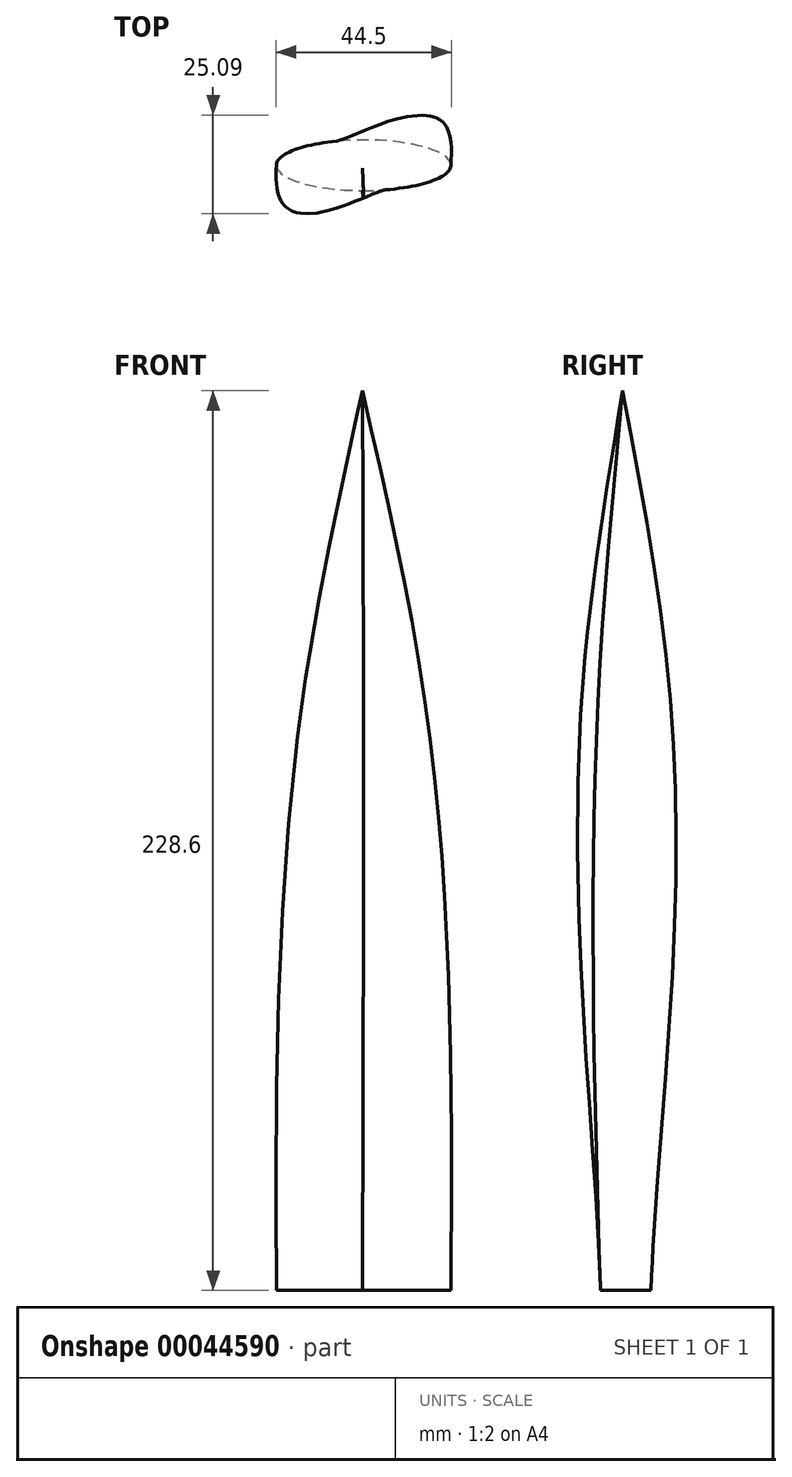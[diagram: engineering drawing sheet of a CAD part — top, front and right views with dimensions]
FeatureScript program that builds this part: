
annotation { "Feature Type Name" : "Feature", "Feature Type Description" : "" }
export const myFeature = defineFeature(function(context is Context, id is Id, definition is map)
    precondition{}
    {
        {
            var Q0;
            Q0=qCreatedBy(makeId("Top.planeOp"),FACE);
            cPlane(context, id + "F0", {"entities" : qUnion([Q0]), "cplaneType" : CPlaneType.OFFSET, "offset" : 152.4 * mm, "width" : 152.4 * mm, "height" : 152.4 * mm});
        }
        {
            var Q0;
            Q0=qCreatedBy(id+"F0.planeOp",FACE);
            cPlane(context, id + "F1", {"entities" : qUnion([Q0]), "cplaneType" : CPlaneType.OFFSET, "offset" : 76.2 * mm, "width" : 152.4 * mm, "height" : 152.4 * mm});
        }
        {
            var Q0;
            Q0=qCreatedBy(makeId("Top.planeOp"),FACE);
            var sketch = newSketch(context, id + "F2", { "sketchPlane" : qUnion([Q0])});
            skEllipse(sketch, "E0", {"center": v(-52.48, 42.01) * mm, "majorRadius": 22.15 * mm, "minorRadius": 6.44 * mm, "majorAxis": v(1, 0)});
            skSolve(sketch);
        }
        {
            var Q0;
            Q0=qCreatedBy(id+"F0.planeOp",FACE);
            var sketch = newSketch(context, id + "F3", { "sketchPlane" : qUnion([Q0])});
            skEllipse(sketch, "E1", {"center": v(-52.48, 42.07) * mm, "majorRadius": 17.88 * mm, "minorRadius": 5.87 * mm, "majorAxis": v(0.83, 0.56)});
            skSolve(sketch);
        }
        {
            var Q0;
            Q0=qCreatedBy(id+"F1.planeOp",FACE);
            var sketch = newSketch(context, id + "F4", { "sketchPlane" : qUnion([Q0])});
            skEllipse(sketch, "E2", {"center": v(-52.77, 41.22) * mm, "majorRadius": 13.98 * mm, "minorRadius": 4.9 * mm, "majorAxis": v(0, 1)});
            skSolve(sketch);
        }
        {
            var Q0;
            Q0=makeQuery(id+"F2.imprint","IMPRINT",FACE,{"disambiguationData":[TD([[makeQuery(id+"F2.imprint","IMPRINT",EDGE,{"derivedFrom":sQuery(id+"F2.wireOp",EDGE,"E0")}),1.0]])]});
            var Q1;
            Q1=makeQuery(id+"F3.imprint","IMPRINT",FACE,{"disambiguationData":[TD([[makeQuery(id+"F3.imprint","IMPRINT",EDGE,{"derivedFrom":sQuery(id+"F3.wireOp",EDGE,"E1")}),1.0]])]});
            var Q2;
            Q2=sQuery(id+"F4.wireOp",VERTEX,"E2.center");
            loft(context, id + "F5", {"sheetProfilesArray" : [{ "sheetProfileEntities" : qUnion([Q0]) }, { "sheetProfileEntities" : qUnion([Q1]) }, { "sheetProfileEntities" : qUnion([Q2]) }]});
        }
    });
